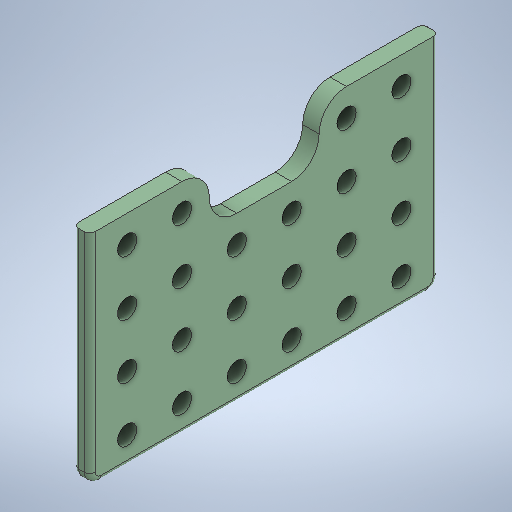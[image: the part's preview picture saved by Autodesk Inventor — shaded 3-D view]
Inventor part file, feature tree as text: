
AUTODESK INVENTOR PART (.ipt)
format: ipt  version: 2025 (Build 290162000, 162)  size: 729,600 bytes
history: native  units: mm
features: fillet x3, extrude x2, sketch x2
ambient origin geometry x8: Origin, YZ Plane, XZ Plane, XY Plane, X Axis, Y Axis, Z Axis, Center Point
bodies: Solide1 (feature_tree)
feature tree (7):
  extrude  "Extrusion1"  Depth=3.0mm
  fillet  "Congé1"  Radius=63.6mm
  fillet  "Congé2"  Radius=40.0mm
  extrude  "Extrusion2"  Depth=2.0mm
  fillet  "Congé3"  Radius=1.0mm
  sketch  "Esquisse1"
  sketch  "Esquisse2"
